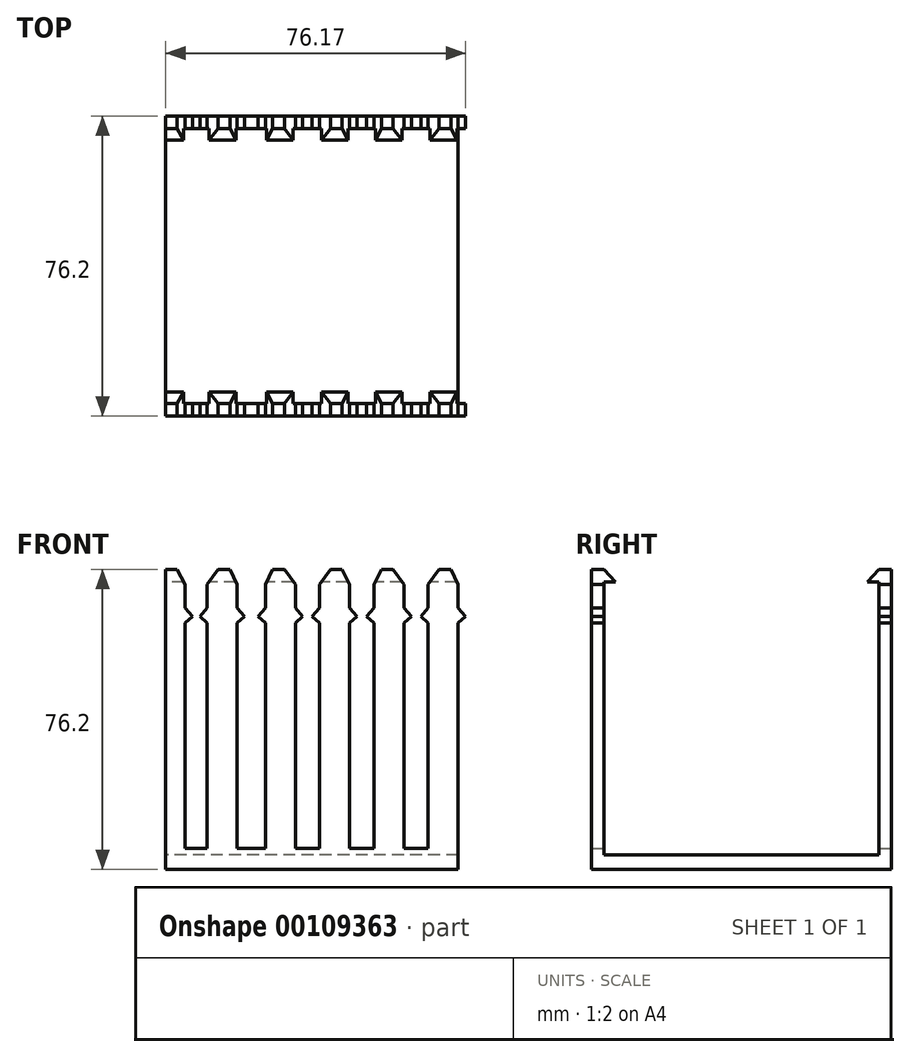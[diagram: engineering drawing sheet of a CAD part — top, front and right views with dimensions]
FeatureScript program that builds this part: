
annotation { "Feature Type Name" : "Feature", "Feature Type Description" : "" }
export const myFeature = defineFeature(function(context is Context, id is Id, definition is map)
    precondition{}
    {
        {
            var Q0;
            Q0=qCreatedBy(makeId("Front.planeOp"),FACE);
            var sketch = newSketch(context, id + "F0", { "sketchPlane" : qUnion([Q0])});
            skLineSegment(sketch, "E0.bottom", {"start": v(-38.1, 38.1) * mm, "end": v(-35.16, 38.1) * mm});
            skLineSegment(sketch, "E0.top", {"start": v(-38.1, -38.1) * mm, "end": v(36.2, -38.1) * mm});
            skLineSegment(sketch, "E0.left", {"start": v(-38.1, 38.1) * mm, "end": v(-38.1, -38.1) * mm});
            skPoint(sketch, "E0.middle", {"position": v(0, 0) * mm});
            skLineSegment(sketch, "E1", {"start": v(-35.16, 38.1) * mm, "end": v(-33.14, 34.25) * mm});
            skLineSegment(sketch, "E2", {"start": v(-33.14, 34.25) * mm, "end": v(-33.14, 28.34) * mm});
            skLineSegment(sketch, "E3", {"start": v(-33.14, 28.34) * mm, "end": v(-31.27, 26.17) * mm});
            skLineSegment(sketch, "E4", {"start": v(-31.27, 26.17) * mm, "end": v(-33.14, 24.57) * mm});
            skLineSegment(sketch, "E5", {"start": v(-33.14, 24.57) * mm, "end": v(-33.14, -32.75) * mm});
            skLineSegment(sketch, "E6", {"start": v(-33.14, -32.75) * mm, "end": v(36.2, -32.75) * mm});
            skLineSegment(sketch, "E7", {"start": v(-33.14, -32.75) * mm, "end": v(-38.1, -32.75) * mm});
            skLineSegment(sketch, "E8", {"start": v(-29.4, 26.17) * mm, "end": v(-27.54, 28.34) * mm});
            skLineSegment(sketch, "E9", {"start": v(-27.54, 28.34) * mm, "end": v(-27.54, 34.25) * mm});
            skLineSegment(sketch, "E10", {"start": v(-27.54, 34.25) * mm, "end": v(-24.74, 38.1) * mm});
            skLineSegment(sketch, "E11", {"start": v(-29.4, 26.17) * mm, "end": v(-27.54, 24.57) * mm});
            skLineSegment(sketch, "E12", {"start": v(-27.54, 24.57) * mm, "end": v(-27.54, -32.75) * mm});
            skLineSegment(sketch, "E13", {"start": v(-24.74, 38.1) * mm, "end": v(-21.79, 38.1) * mm});
            skLineSegment(sketch, "E14", {"start": v(-21.79, 38.1) * mm, "end": v(-19.92, 34.25) * mm});
            skLineSegment(sketch, "E15", {"start": v(-19.92, 34.25) * mm, "end": v(-19.92, 28.34) * mm});
            skLineSegment(sketch, "E16", {"start": v(-19.92, 28.34) * mm, "end": v(-18.06, 26.17) * mm});
            skLineSegment(sketch, "E17", {"start": v(-18.06, 26.17) * mm, "end": v(-19.92, 24.57) * mm});
            skLineSegment(sketch, "E18", {"start": v(-19.92, 24.57) * mm, "end": v(-19.92, -32.75) * mm});
            skLineSegment(sketch, "E19.MirrorCS", {"start": v(-5.16, 34.25) * mm, "end": v(-7.95, 38.1) * mm});
            skLineSegment(sketch, "E20.MirrorCS", {"start": v(-5.16, 28.34) * mm, "end": v(-5.16, 34.25) * mm});
            skLineSegment(sketch, "E21.MirrorCS", {"start": v(-3.3, 26.17) * mm, "end": v(-5.16, 28.34) * mm});
            skLineSegment(sketch, "E22.MirrorCS", {"start": v(-3.3, 26.17) * mm, "end": v(-5.16, 24.57) * mm});
            skLineSegment(sketch, "E23.MirrorCS", {"start": v(-5.16, 24.57) * mm, "end": v(-5.16, -32.75) * mm});
            skLineSegment(sketch, "E24.MirrorCS", {"start": v(-12.77, 24.57) * mm, "end": v(-12.77, -32.75) * mm});
            skLineSegment(sketch, "E25.MirrorCS", {"start": v(-14.64, 26.17) * mm, "end": v(-12.77, 24.57) * mm});
            skLineSegment(sketch, "E26.MirrorCS", {"start": v(-12.77, 28.34) * mm, "end": v(-14.64, 26.17) * mm});
            skLineSegment(sketch, "E27.MirrorCS", {"start": v(-12.77, 34.25) * mm, "end": v(-12.77, 28.34) * mm});
            skLineSegment(sketch, "E28.MirrorCS", {"start": v(-10.9, 38.1) * mm, "end": v(-12.77, 34.25) * mm});
            skLineSegment(sketch, "E29.MirrorCS", {"start": v(-7.95, 38.1) * mm, "end": v(-10.9, 38.1) * mm});
            skLineSegment(sketch, "E30.MirrorCS", {"start": v(-0.9, 26.17) * mm, "end": v(0.98, 28.34) * mm});
            skLineSegment(sketch, "E31.MirrorCS", {"start": v(-0.9, 26.17) * mm, "end": v(0.98, 24.57) * mm});
            skLineSegment(sketch, "E32.MirrorCS", {"start": v(0.98, 24.57) * mm, "end": v(0.98, -32.75) * mm});
            skLineSegment(sketch, "E33.MirrorCS", {"start": v(0.98, 28.34) * mm, "end": v(0.98, 34.25) * mm});
            skLineSegment(sketch, "E34.MirrorCS", {"start": v(0.98, 34.25) * mm, "end": v(3.77, 38.1) * mm});
            skLineSegment(sketch, "E35.MirrorCS", {"start": v(6.73, 38.1) * mm, "end": v(8.6, 34.25) * mm});
            skLineSegment(sketch, "E36.MirrorCS", {"start": v(3.77, 38.1) * mm, "end": v(6.73, 38.1) * mm});
            skLineSegment(sketch, "E37.MirrorCS", {"start": v(8.6, 34.25) * mm, "end": v(8.6, 28.34) * mm});
            skLineSegment(sketch, "E38.MirrorCS", {"start": v(8.6, 28.34) * mm, "end": v(10.46, 26.17) * mm});
            skLineSegment(sketch, "E39.MirrorCS", {"start": v(10.46, 26.17) * mm, "end": v(8.6, 24.57) * mm});
            skLineSegment(sketch, "E40.MirrorCS", {"start": v(8.6, 24.57) * mm, "end": v(8.6, -32.75) * mm});
            skLineSegment(sketch, "E41.MirrorCS", {"start": v(14.84, 28.34) * mm, "end": v(12.98, 26.17) * mm});
            skLineSegment(sketch, "E42.MirrorCS", {"start": v(14.84, 34.25) * mm, "end": v(14.84, 28.34) * mm});
            skLineSegment(sketch, "E43.MirrorCS", {"start": v(16.7, 38.1) * mm, "end": v(14.84, 34.25) * mm});
            skLineSegment(sketch, "E44.MirrorCS", {"start": v(22.46, 34.25) * mm, "end": v(19.66, 38.1) * mm});
            skLineSegment(sketch, "E45.MirrorCS", {"start": v(22.46, 28.34) * mm, "end": v(22.46, 34.25) * mm});
            skLineSegment(sketch, "E46.MirrorCS", {"start": v(24.33, 26.17) * mm, "end": v(22.46, 28.34) * mm});
            skLineSegment(sketch, "E47.MirrorCS", {"start": v(12.98, 26.17) * mm, "end": v(14.84, 24.57) * mm});
            skLineSegment(sketch, "E48.MirrorCS", {"start": v(24.33, 26.17) * mm, "end": v(22.46, 24.57) * mm});
            skLineSegment(sketch, "E49.MirrorCS", {"start": v(22.46, 24.57) * mm, "end": v(22.46, -32.75) * mm});
            skLineSegment(sketch, "E50.MirrorCS", {"start": v(14.84, 24.57) * mm, "end": v(14.84, -32.75) * mm});
            skLineSegment(sketch, "E51.MirrorCS", {"start": v(26.73, 26.17) * mm, "end": v(28.6, 28.34) * mm});
            skLineSegment(sketch, "E52.MirrorCS", {"start": v(26.73, 26.17) * mm, "end": v(28.6, 24.57) * mm});
            skLineSegment(sketch, "E53.MirrorCS", {"start": v(28.6, 24.57) * mm, "end": v(28.6, -32.75) * mm});
            skLineSegment(sketch, "E54.MirrorCS", {"start": v(36.2, 24.57) * mm, "end": v(36.2, -32.75) * mm});
            skLineSegment(sketch, "E55.MirrorCS", {"start": v(38.07, 26.17) * mm, "end": v(36.2, 24.57) * mm});
            skLineSegment(sketch, "E56.MirrorCS", {"start": v(36.2, 28.34) * mm, "end": v(38.07, 26.17) * mm});
            skLineSegment(sketch, "E57.MirrorCS", {"start": v(36.2, 34.25) * mm, "end": v(36.2, 28.34) * mm});
            skLineSegment(sketch, "E58.MirrorCS", {"start": v(34.34, 38.1) * mm, "end": v(36.2, 34.25) * mm});
            skLineSegment(sketch, "E59.MirrorCS", {"start": v(28.6, 34.25) * mm, "end": v(31.4, 38.1) * mm});
            skLineSegment(sketch, "E60.MirrorCS", {"start": v(28.6, 28.34) * mm, "end": v(28.6, 34.25) * mm});
            skLineSegment(sketch, "E61.trimOffspring", {"start": v(6.73, 38.1) * mm, "end": v(3.77, 38.1) * mm});
            skLineSegment(sketch, "E62.trimOffspring", {"start": v(31.4, 38.1) * mm, "end": v(34.34, 38.1) * mm});
            skLineSegment(sketch, "E63.trimOffspring", {"start": v(19.66, 38.1) * mm, "end": v(16.7, 38.1) * mm});
            skLineSegment(sketch, "E64.trimOffspring", {"start": v(34.34, 38.1) * mm, "end": v(31.4, 38.1) * mm});
            skPoint(sketch, "E65.MirrorCS.start.orphan", {"position": v(61.54, 38.1) * mm});
            skPoint(sketch, "E66.orphan", {"position": v(38.1, 38.1) * mm});
            skLineSegment(sketch, "E67", {"start": v(36.2, -32.75) * mm, "end": v(36.2, -38.1) * mm});
            skPoint(sketch, "E68.orphan", {"position": v(38.1, -38.1) * mm});
            skLineSegment(sketch, "E69.trimOffspring", {"start": v(-10.9, 38.1) * mm, "end": v(-7.95, 38.1) * mm});
            skPoint(sketch, "E70.orphan", {"position": v(-14.66, 38.1) * mm});
            skPoint(sketch, "E71.end.orphan", {"position": v(-16.35, 28.8) * mm});
            skPoint(sketch, "E71.start.orphan", {"position": v(-16.35, 26.17) * mm});
            skPoint(sketch, "E72.end.orphan", {"position": v(-2.1, 28.34) * mm});
            skPoint(sketch, "E72.start.orphan", {"position": v(-2.1, 26.17) * mm});
            skPoint(sketch, "E73.end.orphan", {"position": v(11.72, 28.8) * mm});
            skPoint(sketch, "E73.start.orphan", {"position": v(11.72, 26.17) * mm});
            skPoint(sketch, "E74.start.orphan", {"position": v(25.53, 26.17) * mm});
            skSolve(sketch);
        }
        {
            var Q0;
            Q0 = qSketchRegion(id + "F0", true);
            extrude(context, id + "F1", {"entities" : qUnion([Q0]), "depth" : 76.2 * mm});
        }
        {
            var Q0;
            Q0=makeQuery(id+"F1.opExtrude","SWEPT_FACE",FACE,{"disambiguationData":[OSD([sQuery(id+"F0.wireOp",EDGE,"E0.left")])]});
            var sketch = newSketch(context, id + "F2", { "sketchPlane" : qUnion([Q0])});
            skLineSegment(sketch, "E75", {"start": v(0, 41.76) * mm, "end": v(3.18, 41.76) * mm});
            skLineSegment(sketch, "E76", {"start": v(76.2, 43.14) * mm, "end": v(73.03, 43.14) * mm});
            skLineSegment(sketch, "E77.bottom", {"start": v(3.18, 41.76) * mm, "end": v(73.03, 41.76) * mm});
            skLineSegment(sketch, "E77.top", {"start": v(3.18, -34.43) * mm, "end": v(73.03, -34.43) * mm});
            skLineSegment(sketch, "E77.left", {"start": v(3.18, 41.76) * mm, "end": v(3.18, 38.1) * mm});
            skLineSegment(sketch, "E77.right", {"start": v(73.03, 41.76) * mm, "end": v(73.03, 38.1) * mm});
            skLineSegment(sketch, "E78", {"start": v(3.18, 38.1) * mm, "end": v(6.14, 34.97) * mm});
            skLineSegment(sketch, "E79", {"start": v(6.14, 34.97) * mm, "end": v(3.18, 34.97) * mm});
            skLineSegment(sketch, "E80.MirrorCS", {"start": v(70.06, 34.97) * mm, "end": v(73.03, 34.97) * mm});
            skLineSegment(sketch, "E81.MirrorCS", {"start": v(73.03, 38.1) * mm, "end": v(70.06, 34.97) * mm});
            skPoint(sketch, "E82.start.orphan", {"position": v(38.1, 41.76) * mm});
            skLineSegment(sketch, "E83.trimOffspring", {"start": v(3.18, 34.97) * mm, "end": v(3.18, -34.43) * mm});
            skLineSegment(sketch, "E84.trimOffspring", {"start": v(73.03, 34.97) * mm, "end": v(73.03, -34.43) * mm});
            skSolve(sketch);
        }
        {
            var Q0;
            Q0=makeQuery(id+"F2.imprint","IMPRINT",FACE,{"disambiguationData":[TD([[makeQuery(id+"F2.imprint","IMPRINT",EDGE,{"derivedFrom":sQuery(id+"F2.wireOp",EDGE,"E77.top")}),1.0]])]});
            extrude(context, id + "F3", {"entities" : qUnion([Q0]), "operationType" : NewBodyOperationType.REMOVE, "endBound" : BoundingType.THROUGH_ALL, "oppositeDirection" : true, "depth" : 25.4 * mm});
        }
    });
